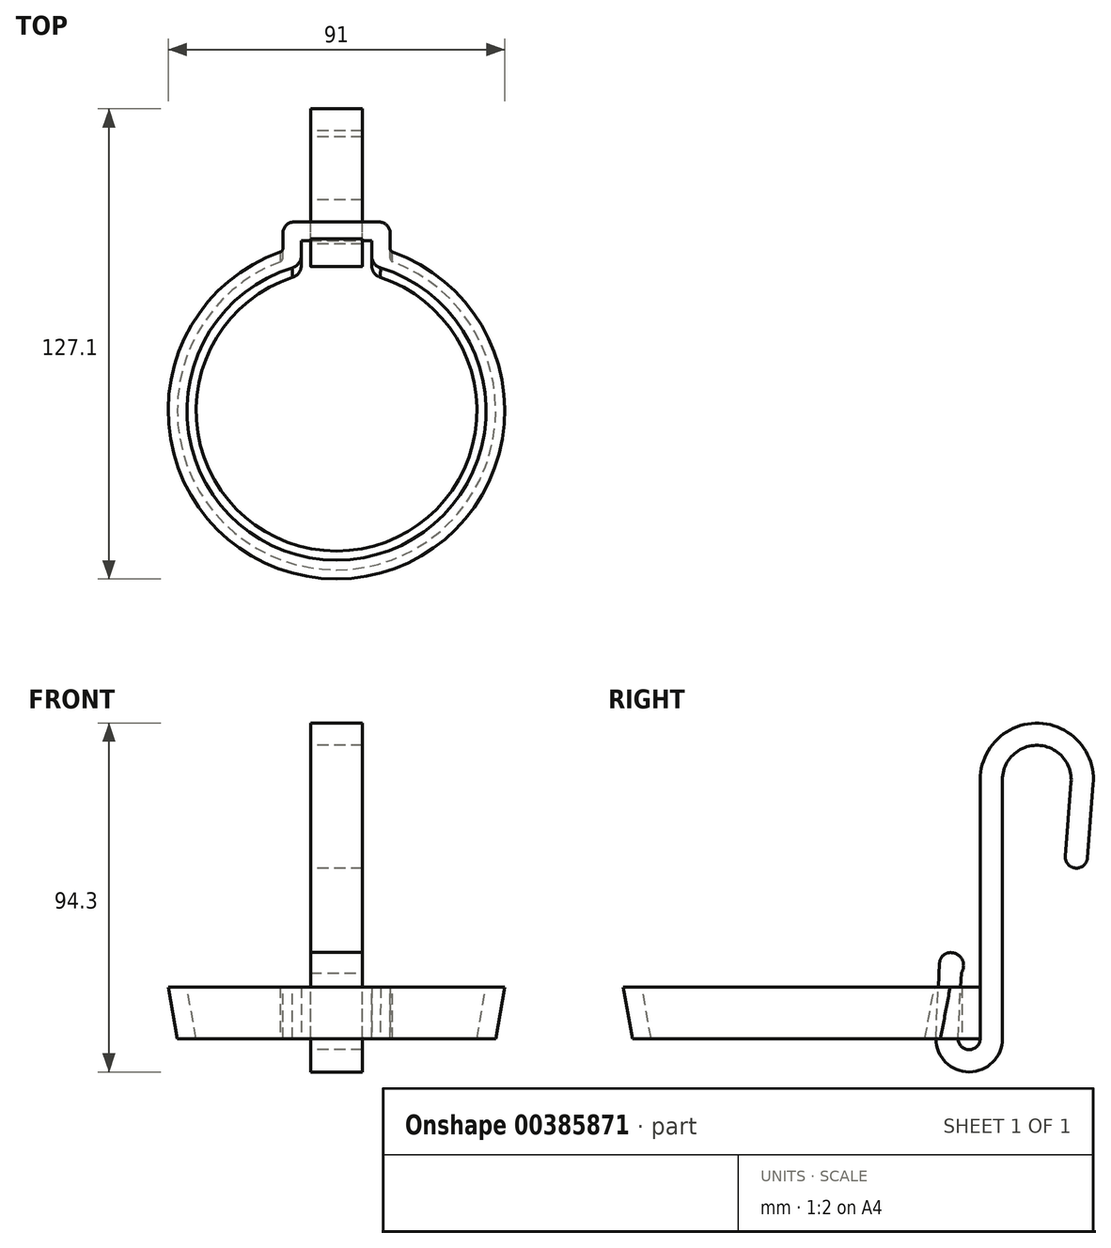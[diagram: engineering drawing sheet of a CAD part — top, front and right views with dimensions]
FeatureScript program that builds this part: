
annotation { "Feature Type Name" : "Feature", "Feature Type Description" : "" }
export const myFeature = defineFeature(function(context is Context, id is Id, definition is map)
    precondition{}
    {
        {
            var Q0;
            Q0=qCreatedBy(makeId("Top.planeOp"),FACE);
            var sketch = newSketch(context, id + "F0", { "sketchPlane" : qUnion([Q0])});
            skCircle(sketch, "E0", {"center": v(0, 0) * mm, "radius": 45.5 * mm});
            skCircle(sketch, "E1", {"center": v(0, 0) * mm, "radius": 40 * mm, "construction": true});
            skSolve(sketch);
        }
        {
            var Q0;
            Q0 = qSketchRegion(id + "F0", true);
            extrude(context, id + "F1", {"entities" : qUnion([Q0]), "oppositeDirection" : true, "depth" : 14 * mm, "hasDraft" : true, "draftAngle" : 10 * degree, "draftPullDirection" : true});
        }
        {
            var Q0;
            Q0=makeQuery(id+"F1.opExtrude","CAP_FACE",FACE,{"disambiguationData":[OSD([sQuery(id+"F0.wireOp",EDGE,"E0")])],"isStart":true});
            var sketch = newSketch(context, id + "F2", { "sketchPlane" : qUnion([Q0])});
            skLineSegment(sketch, "E2.bottom", {"start": v(-14.5, 51) * mm, "end": v(14.5, 51) * mm});
            skLineSegment(sketch, "E2.top", {"start": v(-14.5, 40.51) * mm, "end": v(14.5, 40.51) * mm});
            skLineSegment(sketch, "E2.left", {"start": v(-14.5, 51) * mm, "end": v(-14.5, 40.51) * mm});
            skLineSegment(sketch, "E2.right", {"start": v(14.5, 51) * mm, "end": v(14.5, 40.51) * mm});
            skLineSegment(sketch, "E3", {"start": v(0, 0) * mm, "end": v(0, 40.51) * mm, "construction": true});
            skSolve(sketch);
        }
        {
            var Q0;
            Q0 = qSketchRegion(id + "F2", true);
            var Q1;
            Q1=makeQuery(id+"F1.opExtrude","CAP_FACE",FACE,{"disambiguationData":[OSD([sQuery(id+"F0.wireOp",EDGE,"E0")])],"isStart":false});
            extrude(context, id + "F3", {"entities" : qUnion([Q0]), "operationType" : NewBodyOperationType.ADD, "endBound" : BoundingType.UP_TO_SURFACE, "oppositeDirection" : true, "endBoundEntityFace" : qUnion([Q1]), "depth" : 25 * mm});
        }
        {
            var Q0;
            Q0=makeQuery(id+"F3.opExtrude","SWEPT_EDGE",EDGE,{"disambiguationData":[OSD([sQuery(id+"F2.wireOp",EDGE,"E2.bottom"),sQuery(id+"F2.wireOp",EDGE,"E2.left")])]});
            var Q1;
            Q1=makeQuery(id+"F3.opExtrude","SWEPT_EDGE",EDGE,{"disambiguationData":[OSD([sQuery(id+"F2.wireOp",EDGE,"E2.bottom"),sQuery(id+"F2.wireOp",EDGE,"E2.right")])]});
            fillet(context, id + "F4", {"entities" : qUnion([Q0, Q1]), "radius" : 3 * mm, "tangentPropagation" : true, "allowEdgeOverflow" : false});
        }
        {
            var Q0;
            Q0=makeQuery(id+"F3.boolean.opBoolean","MERGE",FACE,{"derivedFrom":[makeQuery(id+"F1.opExtrude","CAP_FACE",FACE,{"disambiguationData":[OSD([sQuery(id+"F0.wireOp",EDGE,"E0")])],"isStart":true}),makeQuery(id+"F3.opExtrude","CAP_FACE",FACE,{"disambiguationData":[OSD([sQuery(id+"F2.wireOp",EDGE,"E2.bottom"),sQuery(id+"F2.wireOp",EDGE,"E2.top"),sQuery(id+"F2.wireOp",EDGE,"E2.left"),sQuery(id+"F2.wireOp",EDGE,"E2.right")])],"isStart":true})]});
            var Q1;
            {var subQ0=sQuery(id+"F0.wireOp",EDGE,"E0");Q1=makeQuery(id+"F3.boolean.opBoolean","MERGE",FACE,{"derivedFrom":[makeQuery(id+"F1.opExtrude","CAP_FACE",FACE,{"disambiguationData":[OSD([subQ0])],"isStart":false}),makeQuery(id+"F3.opExtrude","CAP_FACE",FACE,{"disambiguationData":[OSD([subQ0])],"isStart":false})]});}
            var Q2;
            Q2=makeQuery(id+"F1.opExtrude","SWEPT_BODY",BODY,{"disambiguationData":[OSD([sQuery(id+"F0.wireOp",EDGE,"E0")])]});
            shell(context, id + "F5", {"entities" : qUnion([Q0, Q1]), "parts" : qUnion([Q2]), "thickness" : 5 * mm});
        }
        {
            var Q0;
            Q0=makeQuery(id+"F3.boolean.opBoolean","INTERSECT",EDGE,{"derivedFrom":[makeQuery(id+"F1.opExtrude","SWEPT_FACE",FACE,{"disambiguationData":[OSD([sQuery(id+"F0.wireOp",EDGE,"E0")])]}),makeQuery(id+"F3.opExtrude","SWEPT_FACE",FACE,{"disambiguationData":[OSD([sQuery(id+"F2.wireOp",EDGE,"E2.left")])]})]});
            var Q1;
            Q1=makeQuery(id+"F3.boolean.opBoolean","INTERSECT",EDGE,{"derivedFrom":[makeQuery(id+"F1.opExtrude","SWEPT_FACE",FACE,{"disambiguationData":[OSD([sQuery(id+"F0.wireOp",EDGE,"E0")])]}),makeQuery(id+"F3.opExtrude","SWEPT_FACE",FACE,{"disambiguationData":[OSD([sQuery(id+"F2.wireOp",EDGE,"E2.right")])]})]});
            fillet(context, id + "F6", {"entities" : qUnion([Q0, Q1]), "radius" : 1 * mm, "tangentPropagation" : true, "allowEdgeOverflow" : false});
        }
        {
            var Q0;
            {var subQ0=sQuery(id+"F2.wireOp",EDGE,"E2.left");var subQ1=sQuery(id+"F0.wireOp",EDGE,"E0");Q0=makeQuery(id+"F5.opShell","OFFSET_EDGE",EDGE,{"disambiguationData":[OSD([subQ1,subQ0]),TDD([makeQuery(id+"F3.boolean.opBoolean","INTERSECT",EDGE,{"derivedFrom":[makeQuery(id+"F1.opExtrude","SWEPT_FACE",FACE,{"disambiguationData":[OSD([subQ1])]}),makeQuery(id+"F3.opExtrude","SWEPT_FACE",FACE,{"disambiguationData":[OSD([subQ0])]})]})])]});}
            var Q1;
            {var subQ0=sQuery(id+"F2.wireOp",EDGE,"E2.right");var subQ1=sQuery(id+"F0.wireOp",EDGE,"E0");Q1=makeQuery(id+"F5.opShell","OFFSET_EDGE",EDGE,{"disambiguationData":[OSD([subQ1,subQ0]),TDD([makeQuery(id+"F3.boolean.opBoolean","INTERSECT",EDGE,{"derivedFrom":[makeQuery(id+"F1.opExtrude","SWEPT_FACE",FACE,{"disambiguationData":[OSD([subQ1])]}),makeQuery(id+"F3.opExtrude","SWEPT_FACE",FACE,{"disambiguationData":[OSD([subQ0])]})]})])]});}
            fillet(context, id + "F7", {"entities" : qUnion([Q0, Q1]), "radius" : (1 + 2.4) * mm, "tangentPropagation" : true, "allowEdgeOverflow" : false});
        }
        {
            var Q0;
            Q0=qCreatedBy(makeId("Right.planeOp"),FACE);
            var sketch = newSketch(context, id + "F8", { "sketchPlane" : qUnion([Q0])});
            skLineSegment(sketch, "E4", {"start": v(57, -14) * mm, "end": v(57, 56) * mm});
            skArc(sketch, "E5", {"start": v(39, -13.55) * mm, "mid": v(47.77, -23) * mm, "end": v(57, -14) * mm});
            skLineSegment(sketch, "E6.0", {"start": v(51, -14) * mm, "end": v(51, 56) * mm});
            skArc(sketch, "E7.0", {"start": v(45, -13.85) * mm, "mid": v(47.92, -17) * mm, "end": v(51, -14) * mm});
            skLineSegment(sketch, "E8", {"start": v(45, -13.85) * mm, "end": v(46, 6.12) * mm});
            skLineSegment(sketch, "E9", {"start": v(39, -13.55) * mm, "end": v(40, 6.42) * mm});
            skArc(sketch, "E10", {"start": v(46, 6.12) * mm, "mid": v(43.15, 9.27) * mm, "end": v(40, 6.42) * mm});
            skArc(sketch, "E11", {"start": v(75.57, 55.27) * mm, "mid": v(66.66, 65.3) * mm, "end": v(57, 56) * mm});
            skArc(sketch, "E12", {"start": v(81.55, 54.8) * mm, "mid": v(66.9, 71.29) * mm, "end": v(51, 56) * mm});
            skLineSegment(sketch, "E13", {"start": v(75.57, 55.27) * mm, "end": v(74, 35.33) * mm});
            skLineSegment(sketch, "E14", {"start": v(81.55, 54.8) * mm, "end": v(80, 34.87) * mm});
            skLineSegment(sketch, "E15", {"start": v(74, 35.33) * mm, "end": v(80, 34.87) * mm, "construction": true});
            skArc(sketch, "E16", {"start": v(74, 35.33) * mm, "mid": v(76.77, 32.1) * mm, "end": v(80, 34.87) * mm});
            skLineSegment(sketch, "E17", {"start": v(51, -14) * mm, "end": v(57, -14) * mm, "construction": true});
            skLineSegment(sketch, "E18", {"start": v(51, 56) * mm, "end": v(57, 56) * mm, "construction": true});
            skLineSegment(sketch, "E19", {"start": v(75.57, 55.27) * mm, "end": v(81.55, 54.8) * mm, "construction": true});
            skLineSegment(sketch, "E20", {"start": v(51, -14) * mm, "end": v(45, -13.85) * mm, "construction": true});
            skSolve(sketch);
        }
        {
            var Q0;
            Q0 = qSketchRegion(id + "F8", true);
            extrude(context, id + "F9", {"entities" : qUnion([Q0]), "endBound" : BoundingType.SYMMETRIC, "depth" : 14 * mm});
        }
        {
            var Q0;
            Q0=makeQuery(id+"F9.opExtrude","CAP_FACE",FACE,{"disambiguationData":[OSD([sQuery(id+"F8.wireOp",EDGE,"E4"),sQuery(id+"F8.wireOp",EDGE,"jrPuZNFN-k8QM-Red7-aA9J-zWhdYr93BGDx"),sQuery(id+"F8.wireOp",EDGE,"E5"),sQuery(id+"F8.wireOp",EDGE,"7e3d26d9-5e12-4922-b482-6ba2a1ab2b7f.0"),sQuery(id+"F8.wireOp",EDGE,"E6.0"),sQuery(id+"F8.wireOp",EDGE,"E7.0"),sQuery(id+"F8.wireOp",EDGE,"E8"),sQuery(id+"F8.wireOp",EDGE,"E9"),sQuery(id+"F8.wireOp",EDGE,"E10"),sQuery(id+"F8.wireOp",EDGE,"TMIjJzHj-1JnN-gwrl-moh8-PzyleGSvfo5R")])],"isStart":false});
            var sketch = newSketch(context, id + "F10", { "sketchPlane" : qUnion([Q0])});
            skLineSegment(sketch, "E21", {"start": v(46, 5.32) * mm, "end": v(46, 1.38) * mm, "construction": true});
            skArc(sketch, "E22", {"start": v(42.85, 2.22) * mm, "mid": v(46.5, 5.6) * mm, "end": v(43.15, 9.27) * mm});
            skPoint(sketch, "E22.startSnap0", {"position": v(42.85, 3.28) * mm});
            skPoint(sketch, "E22.endSnap0", {"position": v(43.15, 9.27) * mm});
            skLineSegment(sketch, "E23", {"start": v(43.15, 9.27) * mm, "end": v(42.85, 2.22) * mm});
            skSolve(sketch);
        }
        {
            var Q0;
            Q0 = qSketchRegion(id + "F10", true);
            var Q1;
            Q1 = qConstructionFilter(qBodyType(qCreatedBy(id + "F10" ,EDGE), BodyType.WIRE), ConstructionObject.NO);
            var Q2;
            Q2=makeQuery(id+"F9.opExtrude","CAP_FACE",FACE,{"disambiguationData":[OSD([sQuery(id+"F8.wireOp",EDGE,"E4"),sQuery(id+"F8.wireOp",EDGE,"jrPuZNFN-k8QM-Red7-aA9J-zWhdYr93BGDx"),sQuery(id+"F8.wireOp",EDGE,"E5"),sQuery(id+"F8.wireOp",EDGE,"7e3d26d9-5e12-4922-b482-6ba2a1ab2b7f.0"),sQuery(id+"F8.wireOp",EDGE,"E6.0"),sQuery(id+"F8.wireOp",EDGE,"E7.0"),sQuery(id+"F8.wireOp",EDGE,"E8"),sQuery(id+"F8.wireOp",EDGE,"E9"),sQuery(id+"F8.wireOp",EDGE,"E10"),sQuery(id+"F8.wireOp",EDGE,"TMIjJzHj-1JnN-gwrl-moh8-PzyleGSvfo5R")])],"isStart":true});
            extrude(context, id + "F11", {"entities" : qUnion([Q0]), "operationType" : NewBodyOperationType.ADD, "surfaceEntities" : qUnion([Q1]), "endBound" : BoundingType.UP_TO_SURFACE, "oppositeDirection" : true, "endBoundEntityFace" : qUnion([Q2]), "depth" : 25 * mm});
        }
    });
